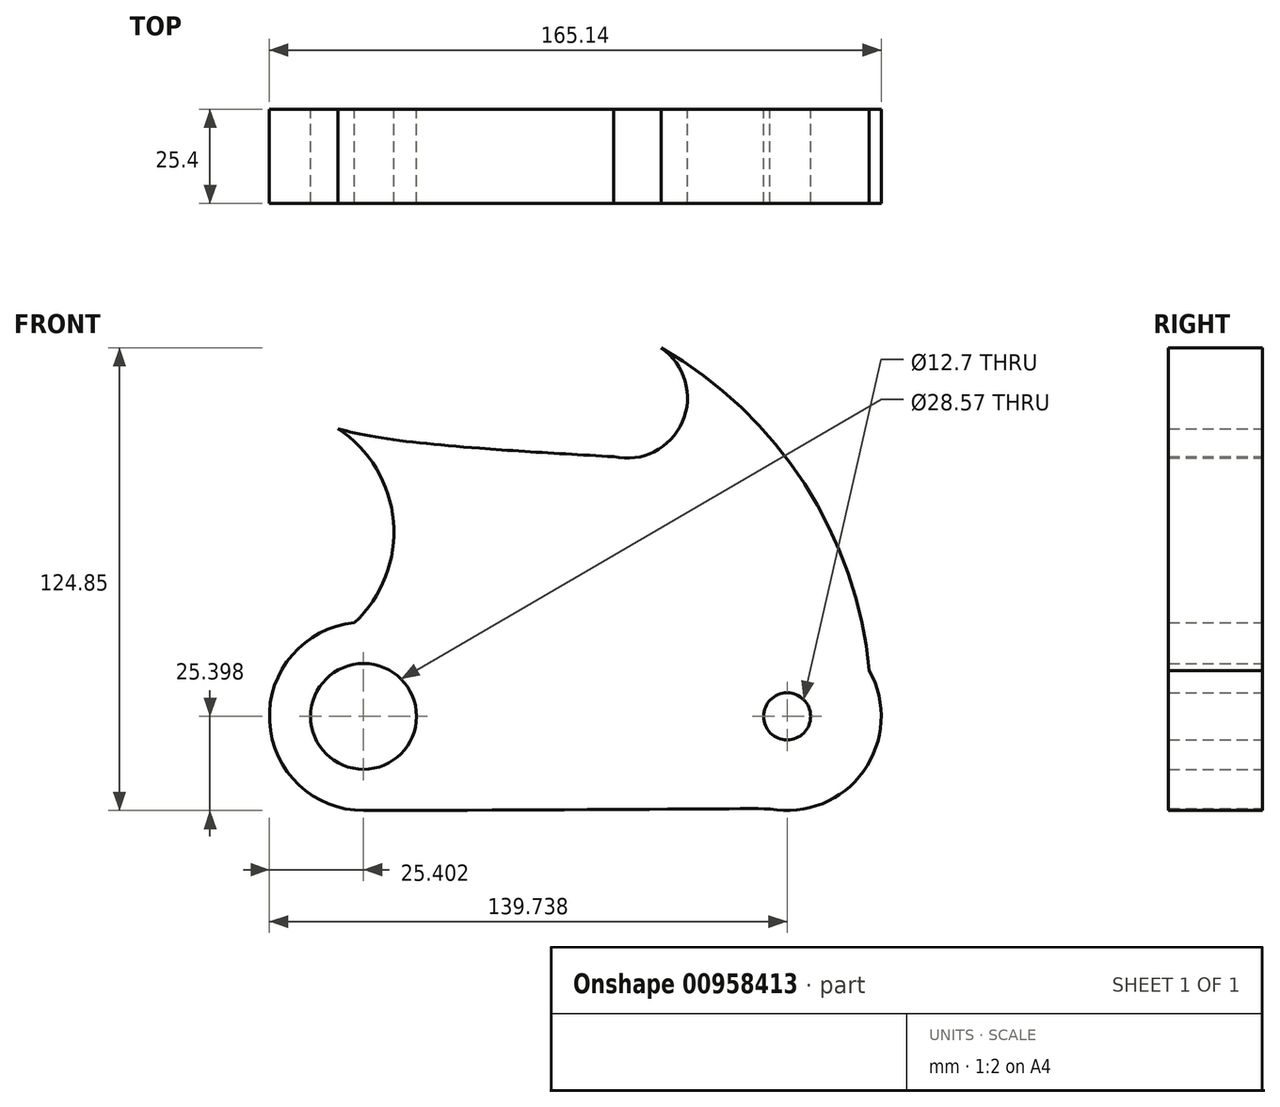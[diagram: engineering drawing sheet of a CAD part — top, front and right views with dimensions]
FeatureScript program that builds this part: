
annotation { "Feature Type Name" : "Feature", "Feature Type Description" : "" }
export const myFeature = defineFeature(function(context is Context, id is Id, definition is map)
    precondition{}
    {
        {
            var Q0;
            Q0=qCreatedBy(makeId("Front.planeOp"),FACE);
            var sketch = newSketch(context, id + "F0", { "sketchPlane" : qUnion([Q0])});
            skCircle(sketch, "E0", {"center": v(-57.17, -51.21) * mm, "radius": 25.4 * mm});
            skCircle(sketch, "E1.MirrorC", {"center": v(57.17, -51.21) * mm, "radius": 25.4 * mm});
            skCircle(sketch, "E2", {"center": v(57.17, -51.21) * mm, "radius": 6.35 * mm});
            skCircle(sketch, "E3", {"center": v(-57.17, -51.21) * mm, "radius": 14.29 * mm});
            skLineSegment(sketch, "E4", {"start": v(0, 0) * mm, "end": v(-53.98, 0) * mm});
            skLineSegment(sketch, "E5.MirrorCS", {"start": v(0, 0) * mm, "end": v(53.98, 0) * mm});
            skArc(sketch, "E6", {"start": v(-59.64, -25.93) * mm, "mid": v(-49.53, 4.62) * mm, "end": v(-69.96, 29.48) * mm});
            skArc(sketch, "E7", {"start": v(79.37, -38.88) * mm, "mid": v(35.43, 40.11) * mm, "end": v(-52.38, 61.56) * mm});
            skArc(sketch, "E8", {"start": v(-52.38, 61.56) * mm, "mid": v(-70.01, 50.37) * mm, "end": v(-69.96, 29.48) * mm});
            skEllipse(sketch, "E9", {"center": v(-28.74, 39.63) * mm, "majorRadius": 38.1 * mm, "minorRadius": 6.35 * mm, "majorAxis": v(1, -0.14)});
            skArc(sketch, "E10", {"start": v(10.37, 18.88) * mm, "mid": v(29.46, 29.68) * mm, "end": v(20.53, 49.72) * mm});
            skFitSpline(sketch, "E11", {"points": [v(10.37, 18.88) * mm, v(-69.96, 29.48) * mm, v(-69.96, 35.12) * mm], "startDerivative": vector(-141.68, 8.02) * mm, "endDerivative": vector(10.6, 28.43) * mm});
            skFitSpline(sketch, "E12", {"points": [v(-57.02, -76.61) * mm, v(52.6, -76.2) * mm, v(52.6, -76.2) * mm], "startDerivative": vector(165.28, 0.18) * mm, "endDerivative": vector(0.48, 0.87) * mm});
            skLineSegment(sketch, "E13", {"start": v(-57.17, -51.21) * mm, "end": v(-13.04, 50.77) * mm});
            skSolve(sketch);
        }
        {
            var Q0;
            {var subQ7=sQuery(id+"F0.wireOp",EDGE,"E12");var subQ8=sQuery(id+"F0.wireOp",EDGE,"E0");var subQ9=makeQuery(id+"F0.imprint","INTERSECT",VERTEX,{"derivedFrom":[subQ8,subQ7]});Q0=makeQuery(id+"F0.imprint","IMPRINT",FACE,{"disambiguationData":[TD([[makeQuery(id+"F0.imprint","IMPRINT",EDGE,{"disambiguationData":[TD([[subQ9,-1.0]])],"derivedFrom":subQ8}),-1.0]])]});}
            var Q1;
            {var subQ0=sQuery(id+"F0.wireOp",EDGE,"E6");var subQ1=sQuery(id+"F0.wireOp",EDGE,"E4");var subQ2=makeQuery(id+"F0.imprint","INTERSECT",VERTEX,{"derivedFrom":[subQ1,subQ0]});Q1=makeQuery(id+"F0.imprint","IMPRINT",FACE,{"disambiguationData":[TD([[makeQuery(id+"F0.imprint","IMPRINT",EDGE,{"disambiguationData":[TD([[subQ2,1.0]])],"derivedFrom":subQ1}),-1.0]])]});}
            var Q2;
            Q2=makeQuery(id+"F0.imprint","IMPRINT",FACE,{"disambiguationData":[TD([[makeQuery(id+"F0.imprint","IMPRINT",EDGE,{"derivedFrom":sQuery(id+"F0.wireOp",EDGE,"E3")}),-1.0]])]});
            var Q3;
            Q3=makeQuery(id+"F0.imprint","IMPRINT",FACE,{"disambiguationData":[TD([[makeQuery(id+"F0.imprint","IMPRINT",EDGE,{"derivedFrom":sQuery(id+"F0.wireOp",EDGE,"E2")}),-1.0]])]});
            var Q4;
            {var subQ1=sQuery(id+"F0.wireOp",EDGE,"E7");var subQ5=sQuery(id+"F0.wireOp",EDGE,"E10");var subQ6=makeQuery(id+"F0.imprint","INTERSECT",VERTEX,{"disambiguationData":[OD(0.0)],"derivedFrom":[subQ1,subQ5]});Q4=makeQuery(id+"F0.imprint","IMPRINT",FACE,{"disambiguationData":[TD([[makeQuery(id+"F0.imprint","IMPRINT",EDGE,{"disambiguationData":[TD([[subQ6,1.0]])],"derivedFrom":subQ1}),1.0]])]});}
            var Q5;
            {var subQ0=sQuery(id+"F0.wireOp",EDGE,"E6");var subQ1=sQuery(id+"F0.wireOp",EDGE,"E0");var subQ2=makeQuery(id+"F0.imprint","INTERSECT",VERTEX,{"derivedFrom":[subQ1,subQ0]});Q5=makeQuery(id+"F0.imprint","IMPRINT",FACE,{"disambiguationData":[TD([[makeQuery(id+"F0.imprint","IMPRINT",EDGE,{"disambiguationData":[TD([[subQ2,1.0]])],"derivedFrom":subQ1}),-1.0]])]});}
            extrude(context, id + "F1", {"entities" : qUnion([Q0, Q1, Q2, Q3, Q4, Q5]), "depth" : 25.4 * mm, "offsetDistance" : 25.4 * mm});
        }
    });
